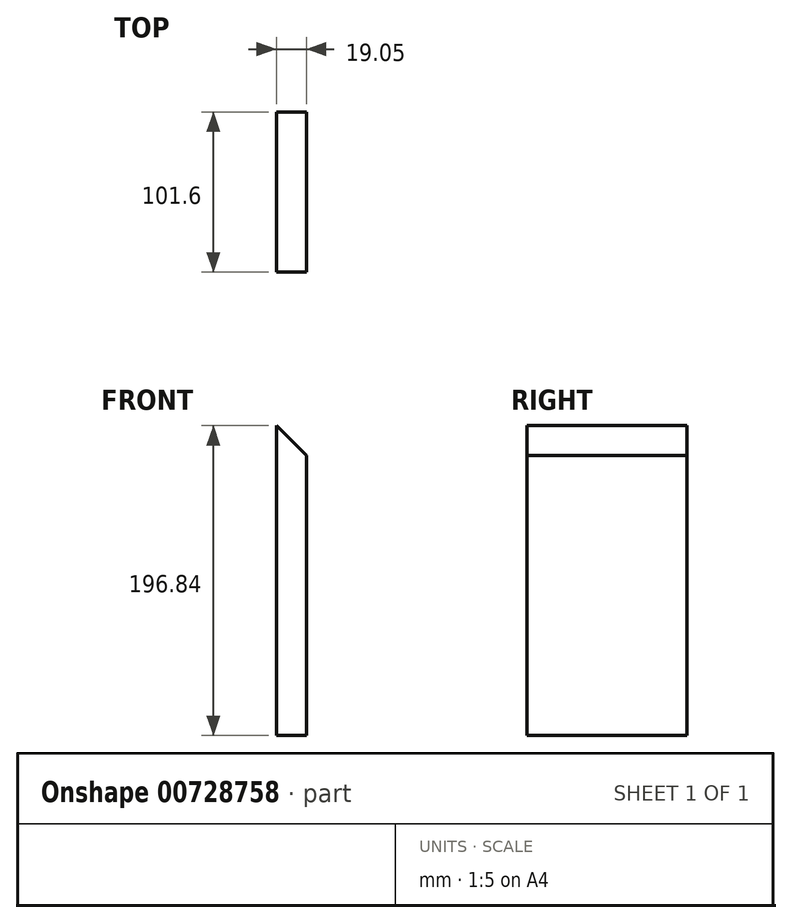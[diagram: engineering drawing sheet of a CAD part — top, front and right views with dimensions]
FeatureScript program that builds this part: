
annotation { "Feature Type Name" : "Feature", "Feature Type Description" : "" }
export const myFeature = defineFeature(function(context is Context, id is Id, definition is map)
    precondition{}
    {
        {
            var Q0;
            Q0=qCreatedBy(makeId("Right.planeOp"),FACE);
            var sketch = newSketch(context, id + "F0", { "sketchPlane" : qUnion([Q0])});
            skLineSegment(sketch, "E0.bottom", {"start": v(44.63, -98.43) * mm, "end": v(-56.97, -98.43) * mm});
            skLineSegment(sketch, "E0.top", {"start": v(44.63, 98.43) * mm, "end": v(-56.97, 98.43) * mm});
            skLineSegment(sketch, "E0.left", {"start": v(44.63, -98.43) * mm, "end": v(44.63, 98.43) * mm});
            skLineSegment(sketch, "E0.right", {"start": v(-56.97, -98.43) * mm, "end": v(-56.97, 98.43) * mm});
            skPoint(sketch, "E0.middle", {"position": v(-6.17, 0) * mm});
            skSolve(sketch);
        }
        {
            var Q0;
            Q0 = qSketchRegion(id + "F0", true);
            extrude(context, id + "F1", {"entities" : qUnion([Q0]), "depth" : 19.05 * mm, "offsetDistance" : 25.4 * mm});
        }
        {
            var Q0;
            Q0=makeQuery(id+"F1.opExtrude","CAP_EDGE",EDGE,{"disambiguationData":[OSD([sQuery(id+"F0.wireOp",EDGE,"E0.top")])],"isStart":false});
            chamfer(context, id + "F2", {"entities" : qUnion([Q0]), "width" : 19.05 * mm, "tangentPropagation" : true});
        }
    });
